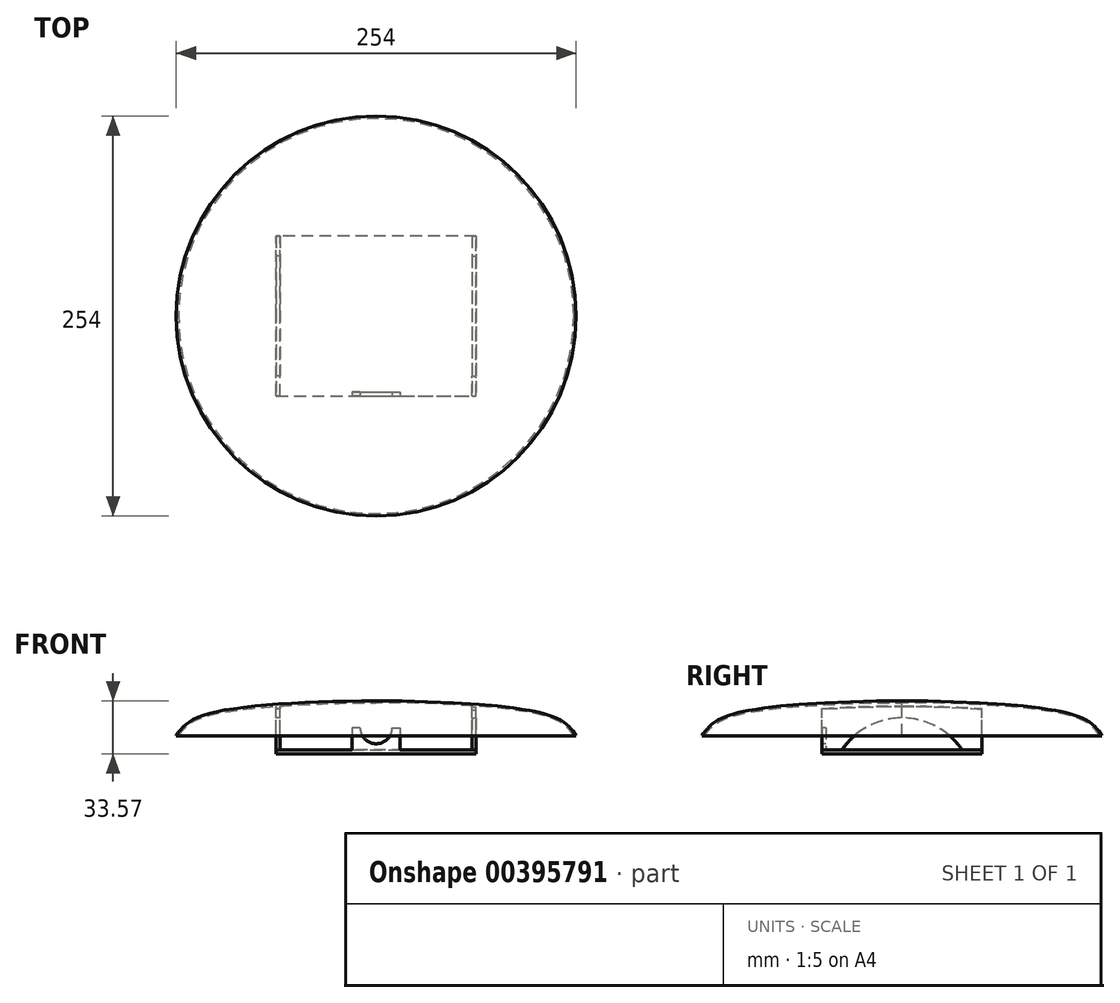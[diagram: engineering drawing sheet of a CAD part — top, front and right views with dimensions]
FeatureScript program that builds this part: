
annotation { "Feature Type Name" : "Feature", "Feature Type Description" : "" }
export const myFeature = defineFeature(function(context is Context, id is Id, definition is map)
    precondition{}
    {
        {
            var Q0;
            Q0=qCreatedBy(makeId("Front.planeOp"),FACE);
            var sketch = newSketch(context, id + "F0", { "sketchPlane" : qUnion([Q0])});
            skPoint(sketch, "E0.orphan", {"position": v(0, 0) * mm});
            skPoint(sketch, "E1.orphan", {"position": v(101.6, 0) * mm});
            skFitSpline(sketch, "E2", {"points": [v(-127, 0) * mm, v(-101.6, 15.24) * mm, v(101.6, 15.24) * mm, v(127, 0) * mm], "startDerivative": vector(60.14, 95.3) * mm, "endDerivative": vector(60.14, -95.3) * mm});
            skLineSegment(sketch, "E3", {"start": v(-127, 0) * mm, "end": v(-125.5, 0) * mm});
            skFitSpline(sketch, "E4.0", {"points": [v(-125.93, -0.68) * mm, v(-125.31, 0.3) * mm, v(-124.07, 2.14) * mm, v(-122, 4.62) * mm, v(-119.5, 6.87) * mm, v(-116.37, 8.94) * mm, v(-112.39, 10.83) * mm, v(-107.35, 12.56) * mm, v(-101.06, 14.13) * mm, v(-93.35, 15.55) * mm, v(-84.4, 16.8) * mm, v(-74.35, 17.88) * mm, v(-63.38, 18.8) * mm, v(-47.71, 19.8) * mm, v(-26.59, 20.64) * mm, v(0, 20.98) * mm, v(26.59, 20.64) * mm, v(47.71, 19.8) * mm, v(63.38, 18.8) * mm, v(74.35, 17.88) * mm, v(84.4, 16.8) * mm, v(93.35, 15.55) * mm, v(101.06, 14.13) * mm, v(107.35, 12.56) * mm, v(112.39, 10.83) * mm, v(116.37, 8.94) * mm, v(119.5, 6.87) * mm, v(122, 4.62) * mm, v(124.07, 2.14) * mm, v(125.31, 0.3) * mm, v(125.93, -0.68) * mm]});
            skLineSegment(sketch, "E5", {"start": v(0, 20.87) * mm, "end": v(0, 22.14) * mm});
            skPoint(sketch, "E6.orphan", {"position": v(-101.6, 0) * mm});
            skSolve(sketch);
        }
        {
            var Q0;
            Q0=makeQuery(id+"F0.imprint","IMPRINT",FACE,{"disambiguationData":[TD([[makeQuery(id+"F0.imprint","IMPRINT",EDGE,{"derivedFrom":sQuery(id+"F0.wireOp",EDGE,"E2")}),-1.0]])]});
            var Q1;
            Q1=sQuery(id+"F0.wireOp",EDGE,"E5");
            revolve(context, id + "F1", {"entities" : qUnion([Q0]), "axis" : qUnion([Q1]), "revolveType" : RevolveType.FULL});
        }
        {
            var Q0;
            Q0=qCreatedBy(makeId("Right.planeOp"),FACE);
            cPlane(context, id + "F2", {"entities" : qUnion([Q0]), "cplaneType" : CPlaneType.OFFSET, "offset" : 63.5 * mm, "width" : 152.4 * mm, "height" : 152.4 * mm});
        }
        {
            var Q0;
            Q0=qCreatedBy(id+"F2.planeOp",FACE);
            var sketch = newSketch(context, id + "F3", { "sketchPlane" : qUnion([Q0])});
            skLineSegment(sketch, "E7.right", {"start": v(-50.8, 0) * mm, "end": v(-50.8, -8.9) * mm});
            skLineSegment(sketch, "E8.left", {"start": v(0, -8.89) * mm, "end": v(0, -8.9) * mm});
            skLineSegment(sketch, "E8.right", {"start": v(50.8, -8.89) * mm, "end": v(50.8, -8.89) * mm});
            skLineSegment(sketch, "E9.right", {"start": v(50.8, 0) * mm, "end": v(50.8, -8.89) * mm});
            skLineSegment(sketch, "E10", {"start": v(-50.8, 0) * mm, "end": v(-50.8, 16.53) * mm});
            skLineSegment(sketch, "E11", {"start": v(50.8, 0) * mm, "end": v(50.8, 16.53) * mm});
            skArc(sketch, "E12", {"start": v(50.8, 16.53) * mm, "mid": v(0, 18.35) * mm, "end": v(-50.8, 16.53) * mm});
            skLineSegment(sketch, "E13", {"start": v(-50.8, -8.9) * mm, "end": v(-38.1, -8.9) * mm});
            skLineSegment(sketch, "E14", {"start": v(50.8, -8.89) * mm, "end": v(38.1, -8.89) * mm});
            skArc(sketch, "E15", {"start": v(38.1, -8.89) * mm, "mid": v(0, 11.36) * mm, "end": v(-38.1, -8.9) * mm});
            skLineSegment(sketch, "E16.trimOffspring", {"start": v(38.1, -8.89) * mm, "end": v(50.8, -8.89) * mm});
            skSolve(sketch);
        }
        {
            var Q0;
            Q0 = qSketchRegion(id + "F3", true);
            extrude(context, id + "F4", {"entities" : qUnion([Q0]), "oppositeDirection" : true, "depth" : 2.54 * mm});
        }
        {
            var Q0;
            Q0=qCreatedBy(id+"F2.planeOp",FACE);
            cPlane(context, id + "F5", {"entities" : qUnion([Q0]), "cplaneType" : CPlaneType.OFFSET, "offset" : 127 * mm, "oppositeDirection" : true, "width" : 152.4 * mm, "height" : 152.4 * mm});
        }
        {
            var Q0;
            Q0=qCreatedBy(id+"F5.planeOp",FACE);
            var sketch = newSketch(context, id + "F6", { "sketchPlane" : qUnion([Q0])});
            skLineSegment(sketch, "E17", {"start": v(50.8, -8.9) * mm, "end": v(38.1, -8.9) * mm});
            skLineSegment(sketch, "E18", {"start": v(50.8, -8.9) * mm, "end": v(50.8, 18) * mm});
            skLineSegment(sketch, "E19", {"start": v(-50.8, -8.9) * mm, "end": v(-50.8, 18) * mm});
            skLineSegment(sketch, "E20", {"start": v(-50.8, -8.9) * mm, "end": v(-38.1, -8.9) * mm});
            skArc(sketch, "E21", {"start": v(38.1, -8.9) * mm, "mid": v(0, 11.34) * mm, "end": v(-38.1, -8.9) * mm});
            skArc(sketch, "E22", {"start": v(50.8, 18) * mm, "mid": v(0, 19.92) * mm, "end": v(-50.8, 18) * mm});
            skSolve(sketch);
        }
        {
            var Q0;
            Q0 = qSketchRegion(id + "F6", true);
            extrude(context, id + "F7", {"entities" : qUnion([Q0]), "operationType" : NewBodyOperationType.ADD, "depth" : 2.54 * mm});
        }
        {
            var Q0;
            Q0=makeQuery(id+"F4.opExtrude","SWEPT_FACE",FACE,{"disambiguationData":[OSD([sQuery(id+"F3.wireOp",EDGE,"E13")])]});
            var sketch = newSketch(context, id + "F8", { "sketchPlane" : qUnion([Q0])});
            skLineSegment(sketch, "E23.left", {"start": v(63.5, 50.8) * mm, "end": v(63.5, 50.8) * mm});
            skLineSegment(sketch, "E23.right", {"start": v(-63.5, 50.8) * mm, "end": v(-63.5, 50.8) * mm});
            skLineSegment(sketch, "E24", {"start": v(63.5, 50.8) * mm, "end": v(63.5, -50.75) * mm});
            skPoint(sketch, "E24.endSnap0", {"position": v(63.5, 44.45) * mm});
            skLineSegment(sketch, "E25", {"start": v(63.5, -50.75) * mm, "end": v(-63.5, -50.82) * mm});
            skLineSegment(sketch, "E26", {"start": v(-63.5, -50.82) * mm, "end": v(-63.5, 50.8) * mm});
            skLineSegment(sketch, "E27", {"start": v(-63.5, 50.8) * mm, "end": v(63.5, 50.8) * mm});
            skSolve(sketch);
        }
        {
            var Q0;
            Q0 = qSketchRegion(id + "F8", true);
            extrude(context, id + "F9", {"entities" : qUnion([Q0]), "depth" : 2.54 * mm});
        }
        {
            var Q0;
            Q0=qCreatedBy(makeId("Front.planeOp"),FACE);
            cPlane(context, id + "F10", {"entities" : qUnion([Q0]), "cplaneType" : CPlaneType.OFFSET, "offset" : 50.8 * mm, "width" : 152.4 * mm, "height" : 152.4 * mm});
        }
        {
            var Q0;
            Q0=qCreatedBy(id+"F10.planeOp",FACE);
            var sketch = newSketch(context, id + "F11", { "sketchPlane" : qUnion([Q0])});
            skArc(sketch, "E28", {"start": v(-10.16, 5.08) * mm, "mid": v(0, -5.08) * mm, "end": v(10.16, 5.08) * mm});
            skLineSegment(sketch, "E29", {"start": v(-10.16, 5.08) * mm, "end": v(-15.24, 5.08) * mm});
            skLineSegment(sketch, "E30", {"start": v(-15.24, 5.08) * mm, "end": v(-15.24, -8.9) * mm});
            skLineSegment(sketch, "E31", {"start": v(10.16, 5.08) * mm, "end": v(15.24, 5.08) * mm});
            skLineSegment(sketch, "E32", {"start": v(15.24, 5.08) * mm, "end": v(15.24, -8.9) * mm});
            skPoint(sketch, "E33.orphan", {"position": v(0, 0) * mm});
            skLineSegment(sketch, "E34", {"start": v(-15.24, -8.9) * mm, "end": v(15.24, -8.9) * mm});
            skSolve(sketch);
        }
        {
            var Q0;
            Q0 = qSketchRegion(id + "F11", true);
            extrude(context, id + "F12", {"entities" : qUnion([Q0]), "operationType" : NewBodyOperationType.ADD, "oppositeDirection" : true, "depth" : 2.54 * mm});
        }
    });
